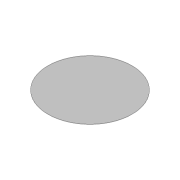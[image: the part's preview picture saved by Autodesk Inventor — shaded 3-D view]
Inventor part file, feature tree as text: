
AUTODESK INVENTOR PART (.ipt)
format: ipt  version: 2022 (Build 260153000, 153)  size: 86,528 bytes
history: native  units: mm
features: extrude x1, sketch x1
ambient origin geometry x8: Origin, YZ Plane, XZ Plane, XY Plane, X Axis, Y Axis, Z Axis, Center Point
bodies: Volumenkörper1 (feature_tree)
feature tree (2):
  extrude  "Extrusion1"  Depth=0.125mm TaperAngle=0.0deg
  sketch  "Skizze1"  dims[d0=25.0mm d1=0.125mm d2=0.0mm]
